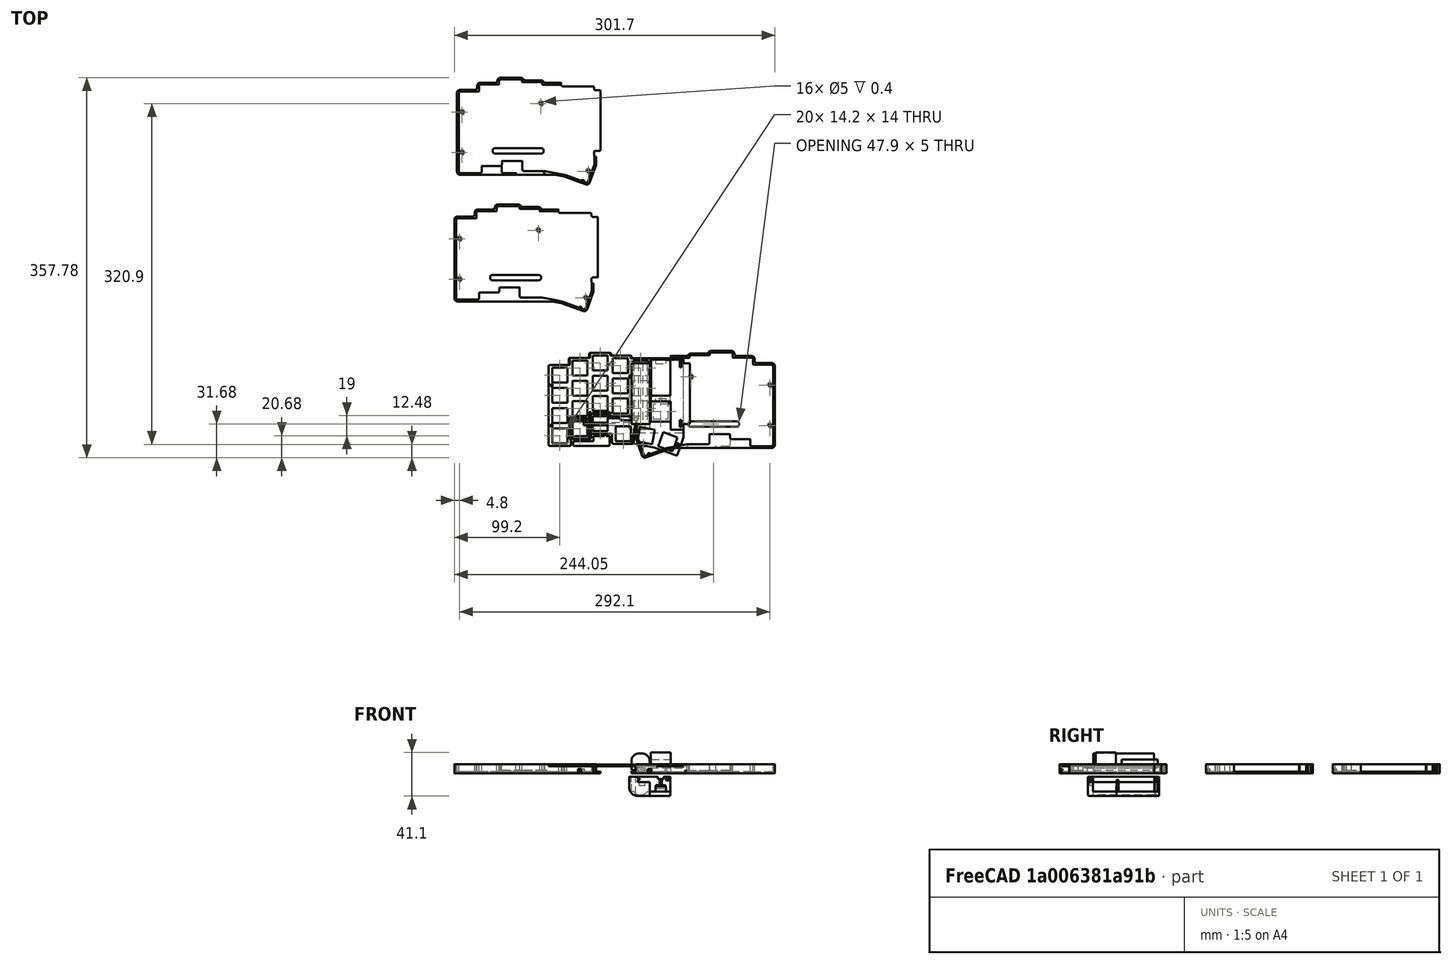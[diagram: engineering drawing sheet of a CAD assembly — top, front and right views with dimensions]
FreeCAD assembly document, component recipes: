
FREECAD ASSEMBLY — COMPONENT RECIPES ("torabo-tsuki-lp-simple-case")

This assembly document has 6 components, labeled P0..P5 below (a component is one placed body or linked part). 1 of them carries a construction recipe — the FreeCAD feature program that regenerates the part from scratch, quoted from this document or its linked companion documents; the rest are supplied as boundary geometry only. No exploded tour is included for this assembly.
COMPONENT P0 — geometry summary ("Body"; its construction recipe is too large to include in this document):
  bounding box: 67.0 x 38.5 x 18.2 mm
  tessellated surface: 6,592 triangles
  volume: 9722 mm^3 (21% of its bounding box)
COMPONENT P1 — recipe-attached ("Body001", modeled in this document).
Construction recipe (the document's own serialized feature program — sketch geometry with constraints, then the solid features built on it; lengths are millimeters unless a unit is written):

FEATURE [Sketcher::SketchObject] Sketch004  label="xy001"
  ArcFitTolerance = 0
  AttachmentSupport = -> [XY_Plane001]
  FullyConstrained = true
  MakeInternals = false
  MapMode = 5
  sketch-geometry (20):
    g0: LineSegment [constr] StartX=9 StartY=-34 StartZ=0 EndX=9 EndY=0 EndZ=0
    g1: LineSegment [constr] StartX=9 StartY=0 StartZ=0 EndX=-9 EndY=0 EndZ=0
    g2: LineSegment [constr] StartX=-9 StartY=0 StartZ=0 EndX=-9 EndY=-34 EndZ=0
    g3: LineSegment [constr] StartX=-9 StartY=-34 StartZ=0 EndX=9 EndY=-34 EndZ=0
    g4: GeomPoint [constr] X=0 Y=-17 Z=0
    g5: LineSegment [constr] StartX=-27.55 StartY=-60.7 StartZ=0 EndX=-27.55 EndY=-3.7 EndZ=0
    g6: LineSegment [constr] StartX=-27.55 StartY=-3.7 StartZ=0 EndX=-10.45 EndY=-3.7 EndZ=0
    g7: LineSegment [constr] StartX=-10.45 StartY=-3.7 StartZ=0 EndX=-10.45 EndY=-60.7 EndZ=0
    g8: LineSegment [constr] StartX=-10.45 StartY=-60.7 StartZ=0 EndX=-27.55 EndY=-60.7 EndZ=0
    g9: GeomPoint [constr] X=-19 Y=-32.2 Z=0
    g10: LineSegment StartX=21.5 StartY=-68.9 StartZ=0 EndX=21.5 EndY=0 EndZ=0
    g11: LineSegment StartX=21.5 StartY=0 StartZ=0 EndX=-21.5 EndY=0 EndZ=0
    g12: LineSegment StartX=-21.5 StartY=0 StartZ=0 EndX=-21.5 EndY=-68.9 EndZ=0
    g13: LineSegment StartX=-21.5 StartY=-68.9 StartZ=0 EndX=21.5 EndY=-68.9 EndZ=0
    g14: GeomPoint [constr] X=0 Y=-34.45 Z=0
    g15: LineSegment [constr] StartX=9.5 StartY=-58.5 StartZ=0 EndX=9.5 EndY=-39.5 EndZ=0
    g16: LineSegment [constr] StartX=9.5 StartY=-39.5 StartZ=0 EndX=-9.5 EndY=-39.5 EndZ=0
    g17: LineSegment [constr] StartX=-9.5 StartY=-39.5 StartZ=0 EndX=-9.5 EndY=-58.5 EndZ=0
    g18: LineSegment [constr] StartX=-9.5 StartY=-58.5 StartZ=0 EndX=9.5 EndY=-58.5 EndZ=0
    g19: GeomPoint [constr] X=0 Y=-49 Z=0
  constraints (52):
    c: Coincident(g0,g1)
    c: Coincident(g1,g2)
    c: Coincident(g2,g3)
    c: Coincident(g3,g0)
    c: Horizontal(g1)
    c: Horizontal(g3)
    c: Vertical(g0)
    c: Vertical(g2)
    c: Symmetric(g1,g0,g4)
    c: PointOnObject(g4,g-2)
    c: Distance(g0) = 34
    c: PointOnObject(g-1,g1)
    c: Distance(g3) = 18
    c: Coincident(g5,g6)
    c: Coincident(g6,g7)
    c: Coincident(g7,g8)
    c: Coincident(g8,g5)
    c: Horizontal(g6)
    c: Horizontal(g8)
    c: Vertical(g5)
    c: Vertical(g7)
    c: Symmetric(g6,g5,g9)
    c: Distance(g6) = 17.1
    c: Distance(g5) = 57
    c: Distance(g9,g-1) = 32.2
    c: Coincident(g10,g11)
    c: Coincident(g11,g12)
    c: Coincident(g12,g13)
    c: Coincident(g13,g10)
    c: Horizontal(g11)
    c: Horizontal(g13)
    c: Vertical(g10)
    c: Vertical(g12)
    c: Symmetric(g11,g10,g14)
    c: PointOnObject(g14,g-2)
    c: PointOnObject(g11,g-1)
    c: Distance(g12,g-2) = 21.5
    c: Distance(g10) = 68.9
    c: Coincident(g15,g16)
    c: Coincident(g16,g17)
    c: Coincident(g17,g18)
    c: Coincident(g18,g15)
    c: Horizontal(g16)
    c: Horizontal(g18)
    c: Vertical(g15)
    c: Vertical(g17)
    c: Symmetric(g16,g15,g19)
    c: PointOnObject(g19,g-2)
    c: Distance(g18) = 19
    c: Distance(g15) = 19
    c: Distance(g19,g-1) = 49
    c: Distance(g9,g-2) = 19
FEATURE [PartDesign::Pad] Pad001
  Direction = (0,0,1)
  Length = 1.6
  Length2 = 10
  Profile = -> Sketch004
  ReferenceAxis = -> Sketch004 [N_Axis]
  Reversed = true
  Suppressed = false
  Type = 0
FEATURE [Sketcher::SketchObject] Sketch005  label="xy002"
  ArcFitTolerance = 0
  AttachmentSupport = -> [XY_Plane001]
  FullyConstrained = true
  MakeInternals = false
  MapMode = 5
  sketch-geometry (20):
    g0: LineSegment StartX=9 StartY=-34 StartZ=0 EndX=9 EndY=0 EndZ=0
    g1: LineSegment StartX=9 StartY=0 StartZ=0 EndX=-9 EndY=0 EndZ=0
    g2: LineSegment StartX=-9 StartY=0 StartZ=0 EndX=-9 EndY=-34 EndZ=0
    g3: LineSegment StartX=-9 StartY=-34 StartZ=0 EndX=9 EndY=-34 EndZ=0
    g4: GeomPoint [constr] X=0 Y=-17 Z=0
    g5: LineSegment [constr] StartX=-27.55 StartY=-60.7 StartZ=0 EndX=-27.55 EndY=-3.7 EndZ=0
    g6: LineSegment [constr] StartX=-27.55 StartY=-3.7 StartZ=0 EndX=-10.45 EndY=-3.7 EndZ=0
    g7: LineSegment [constr] StartX=-10.45 StartY=-3.7 StartZ=0 EndX=-10.45 EndY=-60.7 EndZ=0
    g8: LineSegment [constr] StartX=-10.45 StartY=-60.7 StartZ=0 EndX=-27.55 EndY=-60.7 EndZ=0
    g9: GeomPoint [constr] X=-19 Y=-32.2 Z=0
    g10: LineSegment [constr] StartX=21.5 StartY=-68.9 StartZ=0 EndX=21.5 EndY=0 EndZ=0
    g11: LineSegment [constr] StartX=21.5 StartY=0 StartZ=0 EndX=-21.5 EndY=0 EndZ=0
    g12: LineSegment [constr] StartX=-21.5 StartY=0 StartZ=0 EndX=-21.5 EndY=-68.9 EndZ=0
    g13: LineSegment [constr] StartX=-21.5 StartY=-68.9 StartZ=0 EndX=21.5 EndY=-68.9 EndZ=0
    g14: GeomPoint [constr] X=0 Y=-34.45 Z=0
    g15: LineSegment [constr] StartX=9.5 StartY=-58.5 StartZ=0 EndX=9.5 EndY=-39.5 EndZ=0
    g16: LineSegment [constr] StartX=9.5 StartY=-39.5 StartZ=0 EndX=-9.5 EndY=-39.5 EndZ=0
    g17: LineSegment [constr] StartX=-9.5 StartY=-39.5 StartZ=0 EndX=-9.5 EndY=-58.5 EndZ=0
    g18: LineSegment [constr] StartX=-9.5 StartY=-58.5 StartZ=0 EndX=9.5 EndY=-58.5 EndZ=0
    g19: GeomPoint [constr] X=0 Y=-49 Z=0
  constraints (52):
    c: Coincident(g0,g1)
    c: Coincident(g1,g2)
    c: Coincident(g2,g3)
    c: Coincident(g3,g0)
    c: Horizontal(g1)
    c: Horizontal(g3)
    c: Vertical(g0)
    c: Vertical(g2)
    c: Symmetric(g1,g0,g4)
    c: PointOnObject(g4,g-2)
    c: Distance(g0) = 34
    c: PointOnObject(g-1,g1)
    c: Distance(g3) = 18
    c: Coincident(g5,g6)
    c: Coincident(g6,g7)
    c: Coincident(g7,g8)
    c: Coincident(g8,g5)
    c: Horizontal(g6)
    c: Horizontal(g8)
    c: Vertical(g5)
    c: Vertical(g7)
    c: Symmetric(g6,g5,g9)
    c: Distance(g6) = 17.1
    c: Distance(g5) = 57
    c: Distance(g9,g-1) = 32.2
    c: Coincident(g10,g11)
    c: Coincident(g11,g12)
    c: Coincident(g12,g13)
    c: Coincident(g13,g10)
    c: Horizontal(g11)
    c: Horizontal(g13)
    c: Vertical(g10)
    c: Vertical(g12)
    c: Symmetric(g11,g10,g14)
    c: PointOnObject(g14,g-2)
    c: PointOnObject(g11,g-1)
    c: Distance(g12,g-2) = 21.5
    c: Distance(g10) = 68.9
    c: Coincident(g15,g16)
    c: Coincident(g16,g17)
    c: Coincident(g17,g18)
    c: Coincident(g18,g15)
    c: Horizontal(g16)
    c: Horizontal(g18)
    c: Vertical(g15)
    c: Vertical(g17)
    c: Symmetric(g16,g15,g19)
    c: PointOnObject(g19,g-2)
    c: Distance(g18) = 19
    c: Distance(g15) = 19
    c: Distance(g19,g-1) = 49
    c: Distance(g9,g-2) = 19
FEATURE [PartDesign::Pad] Pad002
  BaseFeature = -> Pad001
  Direction = (0,0,1)
  Length = 6.3
  Length2 = 10
  Profile = -> Sketch005
  ReferenceAxis = -> Sketch005 [N_Axis]
  Suppressed = false
  Type = 0
  expr: Length = Spreadsheet.conn_h + Spreadsheet.controller_h
FEATURE [Sketcher::SketchObject] Sketch006  label="xy003"
  ArcFitTolerance = 0
  AttachmentOffset = pos=(0,0,-3.6) rot=(0,0,1;0rad)
  AttachmentSupport = -> [XY_Plane001]
  FullyConstrained = true
  MakeInternals = false
  MapMode = 5
  Placement = pos=(0,0,-3.6) rot=(0,0,1;0rad)
  expr: .AttachmentOffset.Base.z = -1.6 - 2
  sketch-geometry (20):
    g0: LineSegment [constr] StartX=9 StartY=-34 StartZ=0 EndX=9 EndY=0 EndZ=0
    g1: LineSegment [constr] StartX=9 StartY=0 StartZ=0 EndX=-9 EndY=0 EndZ=0
    g2: LineSegment [constr] StartX=-9 StartY=0 StartZ=0 EndX=-9 EndY=-34 EndZ=0
    g3: LineSegment [constr] StartX=-9 StartY=-34 StartZ=0 EndX=9 EndY=-34 EndZ=0
    g4: GeomPoint [constr] X=0 Y=-17 Z=0
    g5: LineSegment StartX=-27.55 StartY=-60.7 StartZ=0 EndX=-27.55 EndY=-3.7 EndZ=0
    g6: LineSegment StartX=-27.55 StartY=-3.7 StartZ=0 EndX=-10.45 EndY=-3.7 EndZ=0
    g7: LineSegment StartX=-10.45 StartY=-3.7 StartZ=0 EndX=-10.45 EndY=-60.7 EndZ=0
    g8: LineSegment StartX=-10.45 StartY=-60.7 StartZ=0 EndX=-27.55 EndY=-60.7 EndZ=0
    g9: GeomPoint [constr] X=-19 Y=-32.2 Z=0
    g10: LineSegment [constr] StartX=21.5 StartY=-68.9 StartZ=0 EndX=21.5 EndY=0 EndZ=0
    g11: LineSegment [constr] StartX=21.5 StartY=0 StartZ=0 EndX=-21.5 EndY=0 EndZ=0
    g12: LineSegment [constr] StartX=-21.5 StartY=0 StartZ=0 EndX=-21.5 EndY=-68.9 EndZ=0
    g13: LineSegment [constr] StartX=-21.5 StartY=-68.9 StartZ=0 EndX=21.5 EndY=-68.9 EndZ=0
    g14: GeomPoint [constr] X=0 Y=-34.45 Z=0
    g15: LineSegment [constr] StartX=9.5 StartY=-58.5 StartZ=0 EndX=9.5 EndY=-39.5 EndZ=0
    g16: LineSegment [constr] StartX=9.5 StartY=-39.5 StartZ=0 EndX=-9.5 EndY=-39.5 EndZ=0
    g17: LineSegment [constr] StartX=-9.5 StartY=-39.5 StartZ=0 EndX=-9.5 EndY=-58.5 EndZ=0
    g18: LineSegment [constr] StartX=-9.5 StartY=-58.5 StartZ=0 EndX=9.5 EndY=-58.5 EndZ=0
    g19: GeomPoint [constr] X=0 Y=-49 Z=0
  constraints (52):
    c: Coincident(g0,g1)
    c: Coincident(g1,g2)
    c: Coincident(g2,g3)
    c: Coincident(g3,g0)
    c: Horizontal(g1)
    c: Horizontal(g3)
    c: Vertical(g0)
    c: Vertical(g2)
    c: Symmetric(g1,g0,g4)
    c: PointOnObject(g4,g-2)
    c: Distance(g0) = 34
    c: PointOnObject(g-1,g1)
    c: Distance(g3) = 18
    c: Coincident(g5,g6)
    c: Coincident(g6,g7)
    c: Coincident(g7,g8)
    c: Coincident(g8,g5)
    c: Horizontal(g6)
    c: Horizontal(g8)
    c: Vertical(g5)
    c: Vertical(g7)
    c: Symmetric(g6,g5,g9)
    c: Distance(g6) = 17.1
    c: Distance(g5) = 57
    c: Distance(g9,g-1) = 32.2
    c: Coincident(g10,g11)
    c: Coincident(g11,g12)
    c: Coincident(g12,g13)
    c: Coincident(g13,g10)
    c: Horizontal(g11)
    c: Horizontal(g13)
    c: Vertical(g10)
    c: Vertical(g12)
    c: Symmetric(g11,g10,g14)
    c: PointOnObject(g14,g-2)
    c: PointOnObject(g11,g-1)
    c: Distance(g12,g-2) = 21.5
    c: Distance(g10) = 68.9
    c: Coincident(g15,g16)
    c: Coincident(g16,g17)
    c: Coincident(g17,g18)
    c: Coincident(g18,g15)
    c: Horizontal(g16)
    c: Horizontal(g18)
    c: Vertical(g15)
    c: Vertical(g17)
    c: Symmetric(g16,g15,g19)
    c: PointOnObject(g19,g-2)
    c: Distance(g18) = 19
    c: Distance(g15) = 19
    c: Distance(g19,g-1) = 49
    c: Distance(g9,g-2) = 19
FEATURE [PartDesign::Pad] Pad003
  BaseFeature = -> Pad002
  Direction = (0,0,1)
  Length = 15.5
  Length2 = 10
  Profile = -> Sketch006
  ReferenceAxis = -> Sketch006 [N_Axis]
  Suppressed = false
  Type = 0
  expr: Length = Spreadsheet.battery_h
FEATURE [PartDesign::Fillet] Fillet
  Base = -> Pad003 [Edge36,Edge49]
  BaseFeature = -> Pad003
  Radius = 7
  SupportTransform = false
  Suppressed = false
  UseAllEdges = false
FEATURE [Sketcher::SketchObject] Sketch009
  ArcFitTolerance = 0
  AttachmentSupport = -> [XY_Plane001]
  FullyConstrained = false
  MakeInternals = false
  MapMode = 5
  sketch-geometry (9):
    g0: ArcOfCircle CenterX=-19 CenterY=-63.1 CenterZ=0 NormalX=0 NormalY=0 NormalZ=1 AngleXU=0 Radius=1.1 StartAngle=3.14159 EndAngle=6.28319
    g1: ArcOfCircle CenterX=-19 CenterY=-62.3 CenterZ=0 NormalX=0 NormalY=0 NormalZ=1 AngleXU=0 Radius=1.1 StartAngle=-1.8e-15 EndAngle=3.14159
    g2: LineSegment StartX=-17.9 StartY=-63.1 StartZ=0 EndX=-17.9 EndY=-62.3 EndZ=0
    g3: LineSegment StartX=-20.1 StartY=-62.3 StartZ=0 EndX=-20.1 EndY=-63.1 EndZ=0
    g4: LineSegment [constr] StartX=-19 StartY=-63.1 StartZ=0 EndX=-19 EndY=12.3674 EndZ=0
    g5: ArcOfCircle CenterX=-19 CenterY=-1.3 CenterZ=0 NormalX=0 NormalY=0 NormalZ=1 AngleXU=0 Radius=1.1 StartAngle=0 EndAngle=3.14159
    g6: ArcOfCircle CenterX=-19 CenterY=-2.1 CenterZ=0 NormalX=0 NormalY=0 NormalZ=1 AngleXU=0 Radius=1.1 StartAngle=3.14159 EndAngle=6.28319
    g7: LineSegment StartX=-20.1 StartY=-1.3 StartZ=0 EndX=-20.1 EndY=-2.1 EndZ=0
    g8: LineSegment StartX=-17.9 StartY=-2.1 StartZ=0 EndX=-17.9 EndY=-1.3 EndZ=0
  constraints (22):
    c: Tangent(g0,g2) = -1.5708
    c: Tangent(g2,g1) = -1.5708
    c: Tangent(g1,g3) = -1.5708
    c: Tangent(g3,g0) = -1.5708
    c: Equal(g0,g1)
    c: Vertical(g2)
    c: Coincident(g4,g0)
    c: Vertical(g4)
    c: DistanceX(g-2,g0) = -19
    c: Distance(g1,g2) = 2.2
    c: Distance(g1,g0) = 0.8
    c: Tangent(g5,g7) = -1.5708
    c: Tangent(g7,g6) = -1.5708
    c: Tangent(g6,g8) = -1.5708
    c: Tangent(g8,g5) = -1.5708
    c: Equal(g5,g6)
    c: PointOnObject(g5,g4)
    c: PointOnObject(g6,g4)
    c: Distance(g5,g8) = 2.2
    c: Distance(g5,g6) = 0.8
    c: Distance(g5,g-1) = 1.3
    c: Distance(g5,g1) = 61
FEATURE [PartDesign::Pocket] Pocket003
  BaseFeature = -> Fillet
  Direction = (0,0,-1)
  Length = 5
  Length2 = 5
  Profile = -> Sketch009
  ReferenceAxis = -> Sketch009 [N_Axis]
  Suppressed = false
  Type = 1
FEATURE [Sketcher::SketchObject] Sketch010
  ArcFitTolerance = 0
  AttachmentSupport = -> [XY_Plane001]
  FullyConstrained = true
  MakeInternals = false
  MapMode = 5
  expr: Constraints[10] = Sketch006.Constraints[10]
  expr: Constraints[12] = Sketch006.Constraints[12]
  expr: Constraints[22] = Sketch006.Constraints[22]
  expr: Constraints[23] = Sketch006.Constraints[23]
  expr: Constraints[24] = Sketch006.Constraints[24]
  expr: Constraints[36] = Sketch006.Constraints[36]
  expr: Constraints[37] = Sketch006.Constraints[37]
  expr: Constraints[48] = Sketch006.Constraints[48]
  expr: Constraints[49] = Sketch006.Constraints[49]
  expr: Constraints[50] = Sketch006.Constraints[50]
  expr: Constraints[51] = Sketch006.Constraints[51]
  sketch-geometry (20):
    g0: LineSegment [constr] StartX=9 StartY=-34 StartZ=0 EndX=9 EndY=0 EndZ=0
    g1: LineSegment [constr] StartX=9 StartY=0 StartZ=0 EndX=-9 EndY=0 EndZ=0
    g2: LineSegment [constr] StartX=-9 StartY=0 StartZ=0 EndX=-9 EndY=-34 EndZ=0
    g3: LineSegment [constr] StartX=-9 StartY=-34 StartZ=0 EndX=9 EndY=-34 EndZ=0
    g4: GeomPoint [constr] X=0 Y=-17 Z=0
    g5: LineSegment [constr] StartX=-27.55 StartY=-60.7 StartZ=0 EndX=-27.55 EndY=-3.7 EndZ=0
    g6: LineSegment [constr] StartX=-27.55 StartY=-3.7 StartZ=0 EndX=-10.45 EndY=-3.7 EndZ=0
    g7: LineSegment [constr] StartX=-10.45 StartY=-3.7 StartZ=0 EndX=-10.45 EndY=-60.7 EndZ=0
    g8: LineSegment [constr] StartX=-10.45 StartY=-60.7 StartZ=0 EndX=-27.55 EndY=-60.7 EndZ=0
    g9: GeomPoint [constr] X=-19 Y=-32.2 Z=0
    g10: LineSegment [constr] StartX=21.5 StartY=-68.9 StartZ=0 EndX=21.5 EndY=0 EndZ=0
    g11: LineSegment [constr] StartX=21.5 StartY=0 StartZ=0 EndX=-21.5 EndY=0 EndZ=0
    g12: LineSegment [constr] StartX=-21.5 StartY=0 StartZ=0 EndX=-21.5 EndY=-68.9 EndZ=0
    g13: LineSegment [constr] StartX=-21.5 StartY=-68.9 StartZ=0 EndX=21.5 EndY=-68.9 EndZ=0
    g14: GeomPoint [constr] X=0 Y=-34.45 Z=0
    g15: LineSegment StartX=9.5 StartY=-58.5 StartZ=0 EndX=9.5 EndY=-39.5 EndZ=0
    g16: LineSegment StartX=9.5 StartY=-39.5 StartZ=0 EndX=-9.5 EndY=-39.5 EndZ=0
    g17: LineSegment StartX=-9.5 StartY=-39.5 StartZ=0 EndX=-9.5 EndY=-58.5 EndZ=0
    g18: LineSegment StartX=-9.5 StartY=-58.5 StartZ=0 EndX=9.5 EndY=-58.5 EndZ=0
    g19: GeomPoint [constr] X=0 Y=-49 Z=0
  constraints (52):
    c: Coincident(g0,g1)
    c: Coincident(g1,g2)
    c: Coincident(g2,g3)
    c: Coincident(g3,g0)
    c: Horizontal(g1)
    c: Horizontal(g3)
    c: Vertical(g0)
    c: Vertical(g2)
    c: Symmetric(g1,g0,g4)
    c: PointOnObject(g4,g-2)
    c: Distance(g0) = 34
    c: PointOnObject(g-1,g1)
    c: Distance(g3) = 18
    c: Coincident(g5,g6)
    c: Coincident(g6,g7)
    c: Coincident(g7,g8)
    c: Coincident(g8,g5)
    c: Horizontal(g6)
    c: Horizontal(g8)
    c: Vertical(g5)
    c: Vertical(g7)
    c: Symmetric(g6,g5,g9)
    c: Distance(g6) = 17.1
    c: Distance(g5) = 57
    c: Distance(g9,g-1) = 32.2
    c: Coincident(g10,g11)
    c: Coincident(g11,g12)
    c: Coincident(g12,g13)
    c: Coincident(g13,g10)
    c: Horizontal(g11)
    c: Horizontal(g13)
    c: Vertical(g10)
    c: Vertical(g12)
    c: Symmetric(g11,g10,g14)
    c: PointOnObject(g14,g-2)
    c: PointOnObject(g11,g-1)
    c: Distance(g12,g-2) = 21.5
    c: Distance(g10) = 68.9
    c: Coincident(g15,g16)
    c: Coincident(g16,g17)
    c: Coincident(g17,g18)
    c: Coincident(g18,g15)
    c: Horizontal(g16)
    c: Horizontal(g18)
    c: Vertical(g15)
    c: Vertical(g17)
    c: Symmetric(g16,g15,g19)
    c: PointOnObject(g19,g-2)
    c: Distance(g18) = 19
    c: Distance(g15) = 19
    c: Distance(g19,g-1) = 49
    c: Distance(g9,g-2) = 19
FEATURE [PartDesign::Pad] Pad004
  BaseFeature = -> Pocket003
  Direction = (0,0,1)
  Length = 13
  Length2 = 10
  Profile = -> Sketch010
  ReferenceAxis = -> Sketch010 [N_Axis]
  Suppressed = false
  Type = 0
FEATURE [PartDesign::Body] Body001
  AllowCompound = false
  Group = -> [Sketch004,Pad001,Sketch005,Pad002,Sketch006,Pad003,Fillet,Sketch009,Pocket003,Sketch010,Pad004]
  Origin = -> Origin001
  Tip = -> Pad004
COMPONENT P2 — geometry summary ("トラックボール側001"; its construction recipe is too large to include in this document):
  bounding box: 135.0 x 100.6 x 8.5 mm
  tessellated surface: 23,524 triangles
  volume: 22250 mm^3 (19% of its bounding box)
COMPONENT P3 — geometry summary ("キー側001"; its construction recipe is too large to include in this document):
  bounding box: 135.0 x 100.6 x 8.5 mm
  tessellated surface: 22,616 triangles
  volume: 24022 mm^3 (21% of its bounding box)
COMPONENT P4 — geometry summary ("torabo-tsuki-lp-S-bottom 1"; no construction recipe available for this part):
  bounding box: 133.0 x 96.6 x 1.2 mm
  tessellated surface: 1,944 triangles
  volume: 12699 mm^3 (82% of its bounding box)
  symmetry: mirror-symmetric across its z mid-plane
COMPONENT P5 — geometry summary ("torabo-tsuki-lp-S-top 1"; no construction recipe available for this part):
  bounding box: 127.0 x 96.6 x 1.5 mm
  tessellated surface: 2,536 triangles
  volume: 6037 mm^3 (33% of its bounding box)
  symmetry: mirror-symmetric across its z mid-plane
PROVENANCE & LICENSES
A FreeCAD (.FCStd) document from a public repository crawl; recipes are the document's own serialized feature recipes (and, for linked parts, companion documents' recipes).
License: other.
